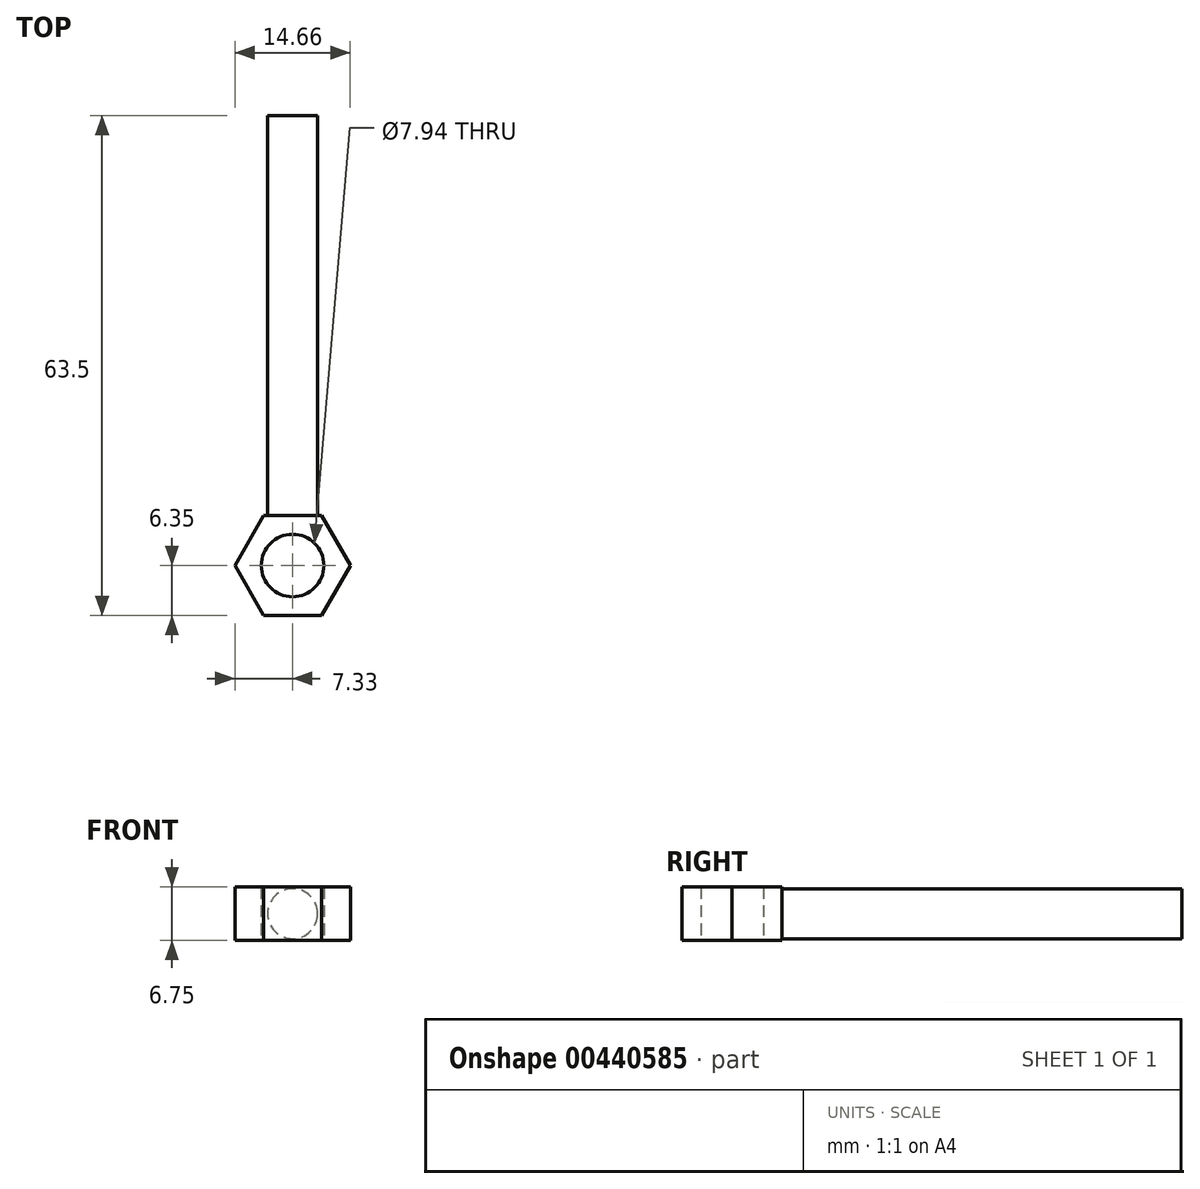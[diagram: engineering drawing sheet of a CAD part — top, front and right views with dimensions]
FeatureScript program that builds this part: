
annotation { "Feature Type Name" : "Feature", "Feature Type Description" : "" }
export const myFeature = defineFeature(function(context is Context, id is Id, definition is map)
    precondition{}
    {
        {
            var Q0;
            Q0=qCreatedBy(makeId("Top.planeOp"),FACE);
            var sketch = newSketch(context, id + "F0", { "sketchPlane" : qUnion([Q0])});
            skCircle(sketch, "E0", {"center": v(0, 0) * mm, "radius": 3.97 * mm});
            skCircle(sketch, "E1.cCircle", {"center": v(0, 0) * mm, "radius": 6.35 * mm, "construction": true});
            skLineSegment(sketch, "E1.0", {"start": v(-3.67, 6.35) * mm, "end": v(3.67, 6.35) * mm});
            skLineSegment(sketch, "E1.1", {"start": v(3.67, 6.35) * mm, "end": v(7.33, 0) * mm});
            skLineSegment(sketch, "E1.2", {"start": v(7.33, 0) * mm, "end": v(3.67, -6.35) * mm});
            skLineSegment(sketch, "E1.3", {"start": v(3.67, -6.35) * mm, "end": v(-3.67, -6.35) * mm});
            skLineSegment(sketch, "E1.4", {"start": v(-3.67, -6.35) * mm, "end": v(-7.33, 0) * mm});
            skLineSegment(sketch, "E1.5", {"start": v(-7.33, 0) * mm, "end": v(-3.67, 6.35) * mm});
            skPoint(sketch, "E1.0.midPoint", {"position": v(0, 6.35) * mm});
            skSolve(sketch);
        }
        {
            var Q0;
            Q0=makeQuery(id+"F0.imprint","IMPRINT",FACE,{"disambiguationData":[TD([[makeQuery(id+"F0.imprint","IMPRINT",EDGE,{"derivedFrom":sQuery(id+"F0.wireOp",EDGE,"E0")}),-1.0]])]});
            extrude(context, id + "F1", {"entities" : qUnion([Q0]), "depth" : 6.75 * mm});
        }
        {
            var Q0;
            Q0=makeQuery(id+"F1.opExtrude","SWEPT_FACE",FACE,{"disambiguationData":[OSD([sQuery(id+"F0.wireOp",EDGE,"E1.0")])]});
            var sketch = newSketch(context, id + "F2", { "sketchPlane" : qUnion([Q0])});
            skCircle(sketch, "E2", {"center": v(0, 3.37) * mm, "radius": 3.18 * mm});
            skPoint(sketch, "E2.centerSnap0", {"position": v(-3.67, 3.37) * mm});
            skSolve(sketch);
        }
        {
            var Q0;
            Q0 = qSketchRegion(id + "F2", true);
            extrude(context, id + "F3", {"entities" : qUnion([Q0]), "operationType" : NewBodyOperationType.ADD, "depth" : 50.8 * mm});
        }
    });
